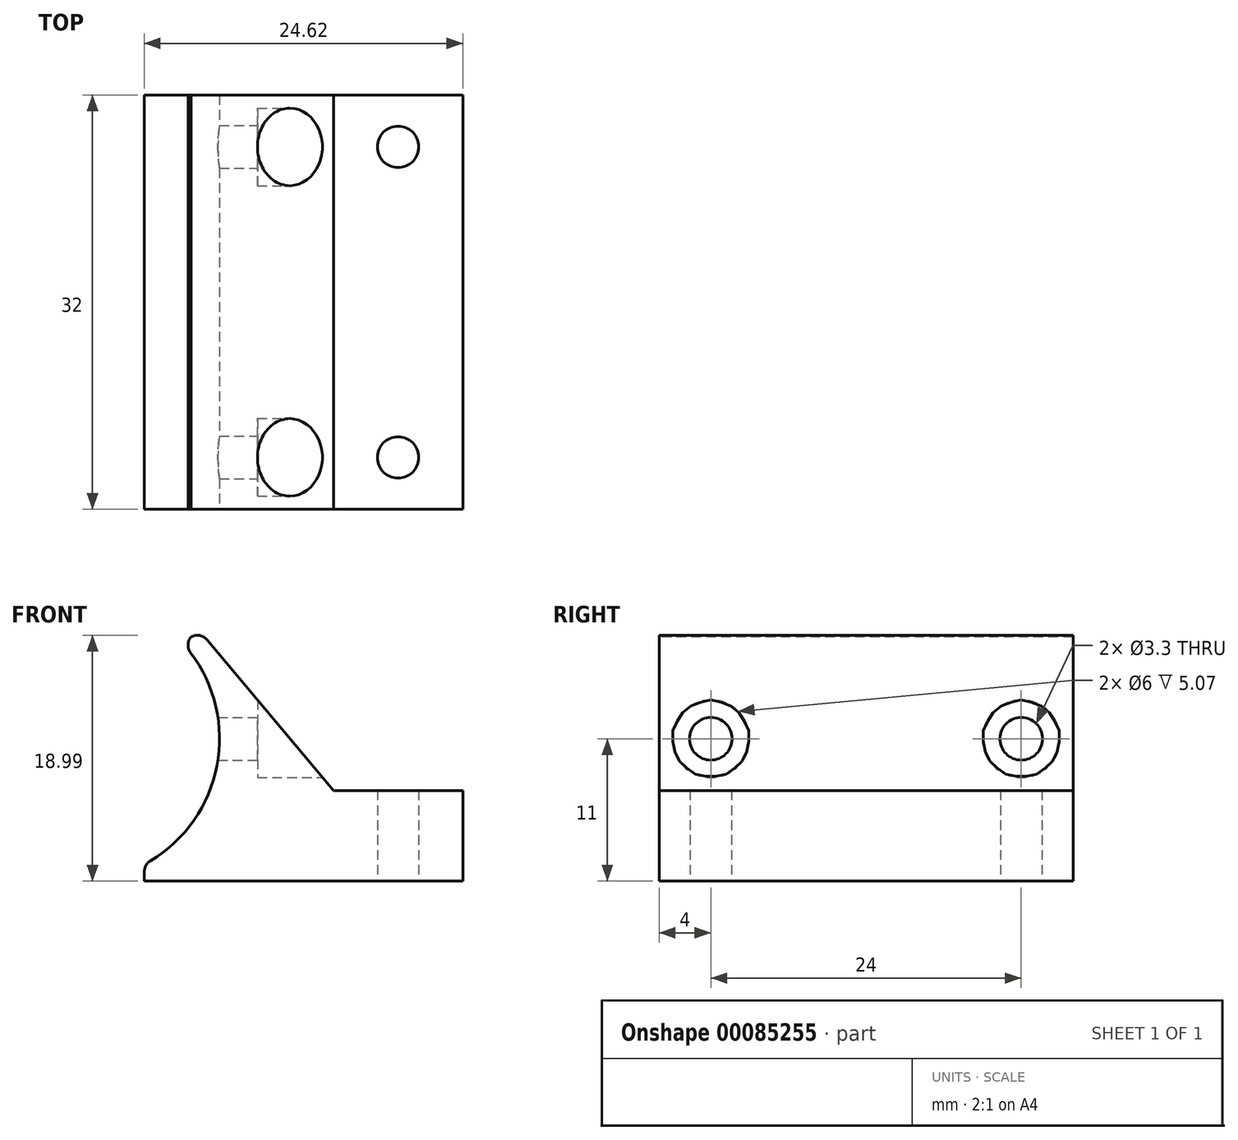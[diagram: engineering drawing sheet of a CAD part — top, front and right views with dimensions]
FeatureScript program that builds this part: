
annotation { "Feature Type Name" : "Feature", "Feature Type Description" : "" }
export const myFeature = defineFeature(function(context is Context, id is Id, definition is map)
    precondition{}
    {
        {
            var Q0;
            Q0=qCreatedBy(makeId("Top.planeOp"),FACE);
            var sketch = newSketch(context, id + "F0", { "sketchPlane" : qUnion([Q0])});
            skCircle(sketch, "E0", {"center": v(-5, 28) * mm, "radius": 2.58 * mm, "construction": true});
            skCircle(sketch, "E1", {"center": v(-5, 28) * mm, "radius": 1.6 * mm});
            skCircle(sketch, "E2", {"center": v(-5, 4) * mm, "radius": 2.58 * mm, "construction": true});
            skCircle(sketch, "E3", {"center": v(-5, 4) * mm, "radius": 1.6 * mm});
            skLineSegment(sketch, "E4", {"start": v(-5, 56.36) * mm, "end": v(-5, -15.86) * mm, "construction": true});
            skLineSegment(sketch, "E5.bottom", {"start": v(0, 32) * mm, "end": v(-52.05, 32) * mm});
            skLineSegment(sketch, "E5.top", {"start": v(0, 0) * mm, "end": v(-52.05, 0) * mm});
            skLineSegment(sketch, "E5.left", {"start": v(0, 32) * mm, "end": v(0, 0) * mm});
            skLineSegment(sketch, "E5.right", {"start": v(-52.05, 32) * mm, "end": v(-52.05, 0) * mm});
            skSolve(sketch);
        }
        {
            var Q0;
            Q0=qCreatedBy(makeId("Front.planeOp"),FACE);
            var sketch = newSketch(context, id + "F1", { "sketchPlane" : qUnion([Q0])});
            skLineSegment(sketch, "E6", {"start": v(17.17, 0) * mm, "end": v(-62.4, 0) * mm, "construction": true});
            skPoint(sketch, "E7", {"position": v(0, 0) * mm});
            skPoint(sketch, "E8", {"position": v(-52.05, 0) * mm});
            skLineSegment(sketch, "E9", {"start": v(0, 0) * mm, "end": v(0, 7) * mm});
            skLineSegment(sketch, "E10", {"start": v(0, 7) * mm, "end": v(-10, 7) * mm});
            skLineSegment(sketch, "E11", {"start": v(-10, 7) * mm, "end": v(-29.8, 30.6) * mm});
            skLineSegment(sketch, "E12", {"start": v(-29.8, 30.6) * mm, "end": v(-29.8, 26.14) * mm});
            skLineSegment(sketch, "E13", {"start": v(-29.8, 0) * mm, "end": v(0, 0) * mm});
            skCircle(sketch, "E14", {"center": v(-29.8, 11) * mm, "radius": 11 * mm});
            skLineSegment(sketch, "E15", {"start": v(-29.8, 26.14) * mm, "end": v(-26.06, 26.14) * mm});
            skLineSegment(sketch, "E16", {"start": v(-29.8, 26.14) * mm, "end": v(-29.8, 0) * mm});
            skLineSegment(sketch, "E17", {"start": v(-29.8, 11) * mm, "end": v(-15.85, 11) * mm, "construction": true});
            skPoint(sketch, "E18", {"position": v(-18.8, 11) * mm});
            skLineSegment(sketch, "E19", {"start": v(-25.17, 20.97) * mm, "end": v(-23.15, 22.67) * mm});
            skLineSegment(sketch, "E20", {"start": v(-24.62, 1.3) * mm, "end": v(-24.62, 0) * mm});
            skLineSegment(sketch, "E21", {"start": v(-24.16, 21.82) * mm, "end": v(-18, 14.48) * mm});
            skLineSegment(sketch, "E22", {"start": v(-20.4, 19.4) * mm, "end": v(-21.64, 18.37) * mm});
            skSolve(sketch);
        }
        {
            var Q0;
            Q0=makeQuery(id+"F1.imprint","IMPRINT",FACE,{"disambiguationData":[TD([[makeQuery(id+"F1.imprint","IMPRINT",EDGE,{"derivedFrom":sQuery(id+"F1.wireOp",EDGE,"E9")}),1.0]])]});
            extrude(context, id + "F2", {"entities" : qUnion([Q0]), "oppositeDirection" : true, "depth" : 32 * mm});
        }
        {
            var Q0;
            Q0=makeQuery(id+"F0.imprint","IMPRINT",FACE,{"disambiguationData":[TD([[makeQuery(id+"F0.imprint","IMPRINT",EDGE,{"derivedFrom":sQuery(id+"F0.wireOp",EDGE,"E3")}),1.0]])]});
            var Q1;
            Q1=makeQuery(id+"F0.imprint","IMPRINT",FACE,{"disambiguationData":[TD([[makeQuery(id+"F0.imprint","IMPRINT",EDGE,{"derivedFrom":sQuery(id+"F0.wireOp",EDGE,"E1")}),1.0]])]});
            extrude(context, id + "F3", {"entities" : qUnion([Q0, Q1]), "operationType" : NewBodyOperationType.REMOVE, "depth" : 25 * mm});
        }
        {
            var Q0;
            Q0=qCreatedBy(makeId("Right.planeOp"),FACE);
            var sketch = newSketch(context, id + "F4", { "sketchPlane" : qUnion([Q0])});
            skLineSegment(sketch, "E23", {"start": v(0, 11) * mm, "end": v(32, 11) * mm});
            skPoint(sketch, "E24", {"position": v(4, 11) * mm});
            skPoint(sketch, "E25", {"position": v(28, 11) * mm});
            skLineSegment(sketch, "E26", {"start": v(16, 11) * mm, "end": v(16, 19.6) * mm, "construction": true});
            skSolve(sketch);
        }
        {
            var Q0;
            Q0=sQuery(id+"F4.wireOp",VERTEX,"E24");
            var Q1;
            Q1=sQuery(id+"F4.wireOp",VERTEX,"E25");
            var Q2;
            Q2=makeQuery(id+"F2.opExtrude","SWEPT_BODY",BODY,{"disambiguationData":[OSD([sQuery(id+"F1.wireOp",EDGE,"E9"),sQuery(id+"F1.wireOp",EDGE,"E10"),sQuery(id+"F1.wireOp",EDGE,"E11"),sQuery(id+"F1.wireOp",EDGE,"E13"),sQuery(id+"F1.wireOp",EDGE,"E14"),sQuery(id+"F1.wireOp",EDGE,"E15"),sQuery(id+"F1.wireOp",EDGE,"E16")])]});
            hole(context, id + "F5", {"style" : HoleStyle.C_BORE, "endStyle" : HoleEndStyle.BLIND, "holeDiameter" : 3.3 * mm, "cBoreDiameter" : 6 * mm, "cBoreDepth" : 0 * mm, "holeDepth" : 20 * mm, "locations" : qUnion([Q0, Q1]), "scope" : qUnion([Q2])});
        }
        {
            var Q0;
            Q0=makeQuery(id+"F2.opExtrude","SWEPT_EDGE",EDGE,{"disambiguationData":[OSD([sQuery(id+"F1.wireOp",EDGE,"E14"),sQuery(id+"F1.wireOp",EDGE,"E20")])]});
            var Q1;
            Q1=makeQuery(id+"F2.opExtrude","SWEPT_EDGE",EDGE,{"disambiguationData":[OSD([sQuery(id+"F1.wireOp",EDGE,"E14"),sQuery(id+"F1.wireOp",EDGE,"E22")])]});
            var Q2;
            Q2=makeQuery(id+"F2.opExtrude","SWEPT_EDGE",EDGE,{"disambiguationData":[OSD([sQuery(id+"F1.wireOp",EDGE,"E11"),sQuery(id+"F1.wireOp",EDGE,"E22")])]});
            fillet(context, id + "F6", {"entities" : qUnion([Q0, Q1, Q2]), "radius" : 1 * mm, "tangentPropagation" : true, "allowEdgeOverflow" : false});
        }
    });
